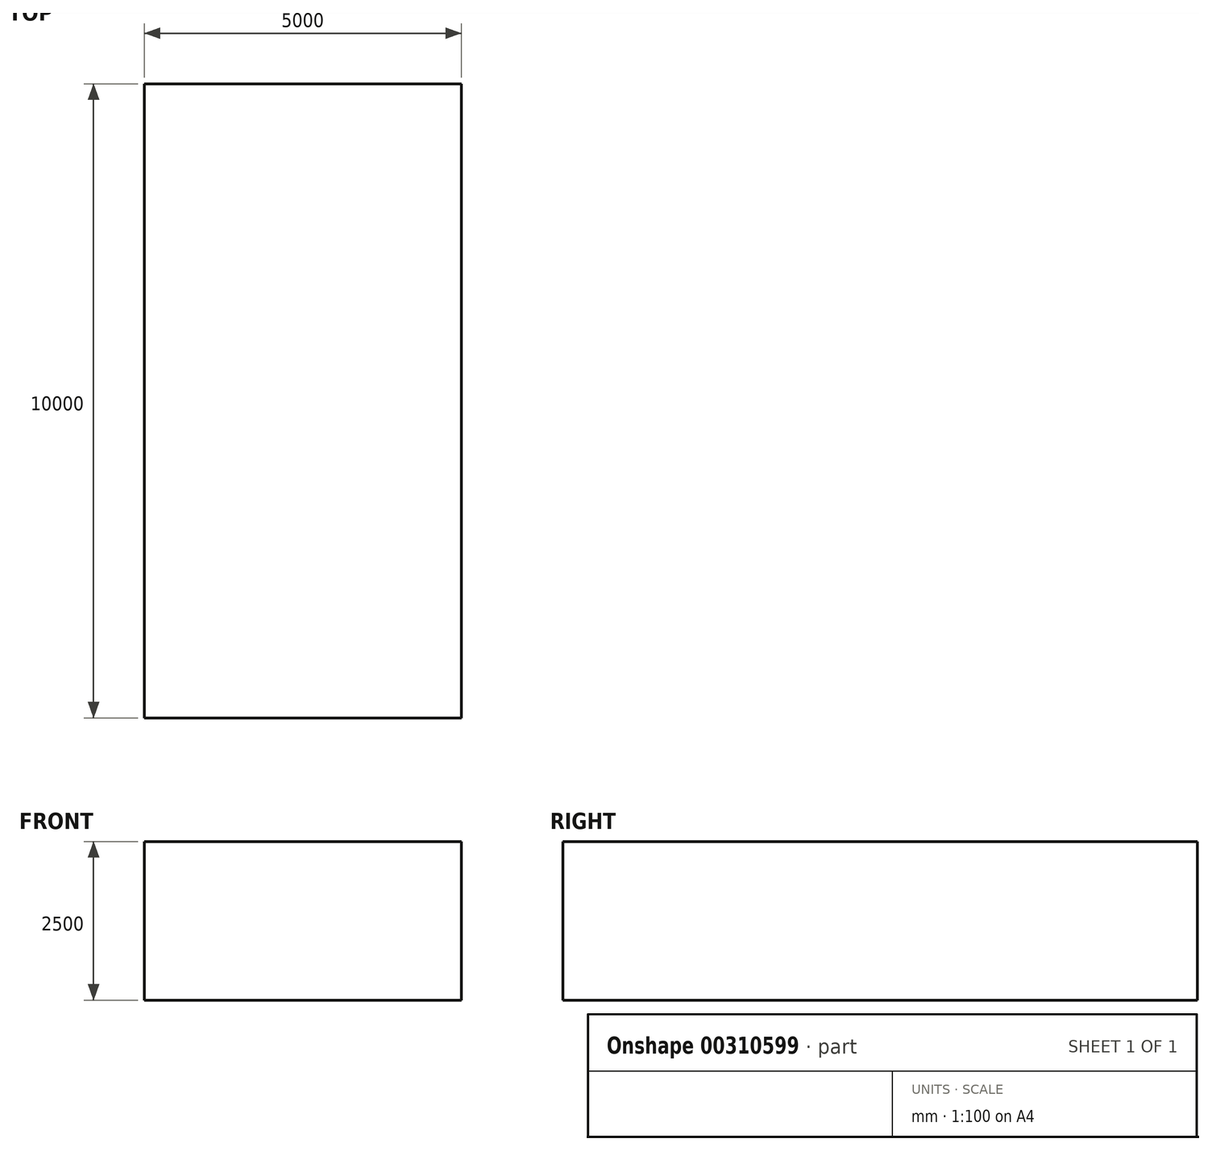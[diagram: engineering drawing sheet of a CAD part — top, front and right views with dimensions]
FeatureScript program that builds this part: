
annotation { "Feature Type Name" : "Feature", "Feature Type Description" : "" }
export const myFeature = defineFeature(function(context is Context, id is Id, definition is map)
    precondition{}
    {
        {
            var Q0;
            Q0=qCreatedBy(makeId("Front.planeOp"),FACE);
            var sketch = newSketch(context, id + "F0", { "sketchPlane" : qUnion([Q0])});
            skLineSegment(sketch, "E0.bottom", {"start": v(-2126.47, 1251.46) * mm, "end": v(2873.53, 1251.46) * mm});
            skLineSegment(sketch, "E0.top", {"start": v(-2126.47, -1248.54) * mm, "end": v(2873.53, -1248.54) * mm});
            skLineSegment(sketch, "E0.left", {"start": v(-2126.47, 1251.46) * mm, "end": v(-2126.47, -1248.54) * mm});
            skLineSegment(sketch, "E0.right", {"start": v(2873.53, 1251.46) * mm, "end": v(2873.53, -1248.54) * mm});
            skSolve(sketch);
        }
        {
            var Q0;
            Q0 = qSketchRegion(id + "F0", true);
            extrude(context, id + "F1", {"entities" : qUnion([Q0]), "depth" : 10000 * mm});
        }
    });
